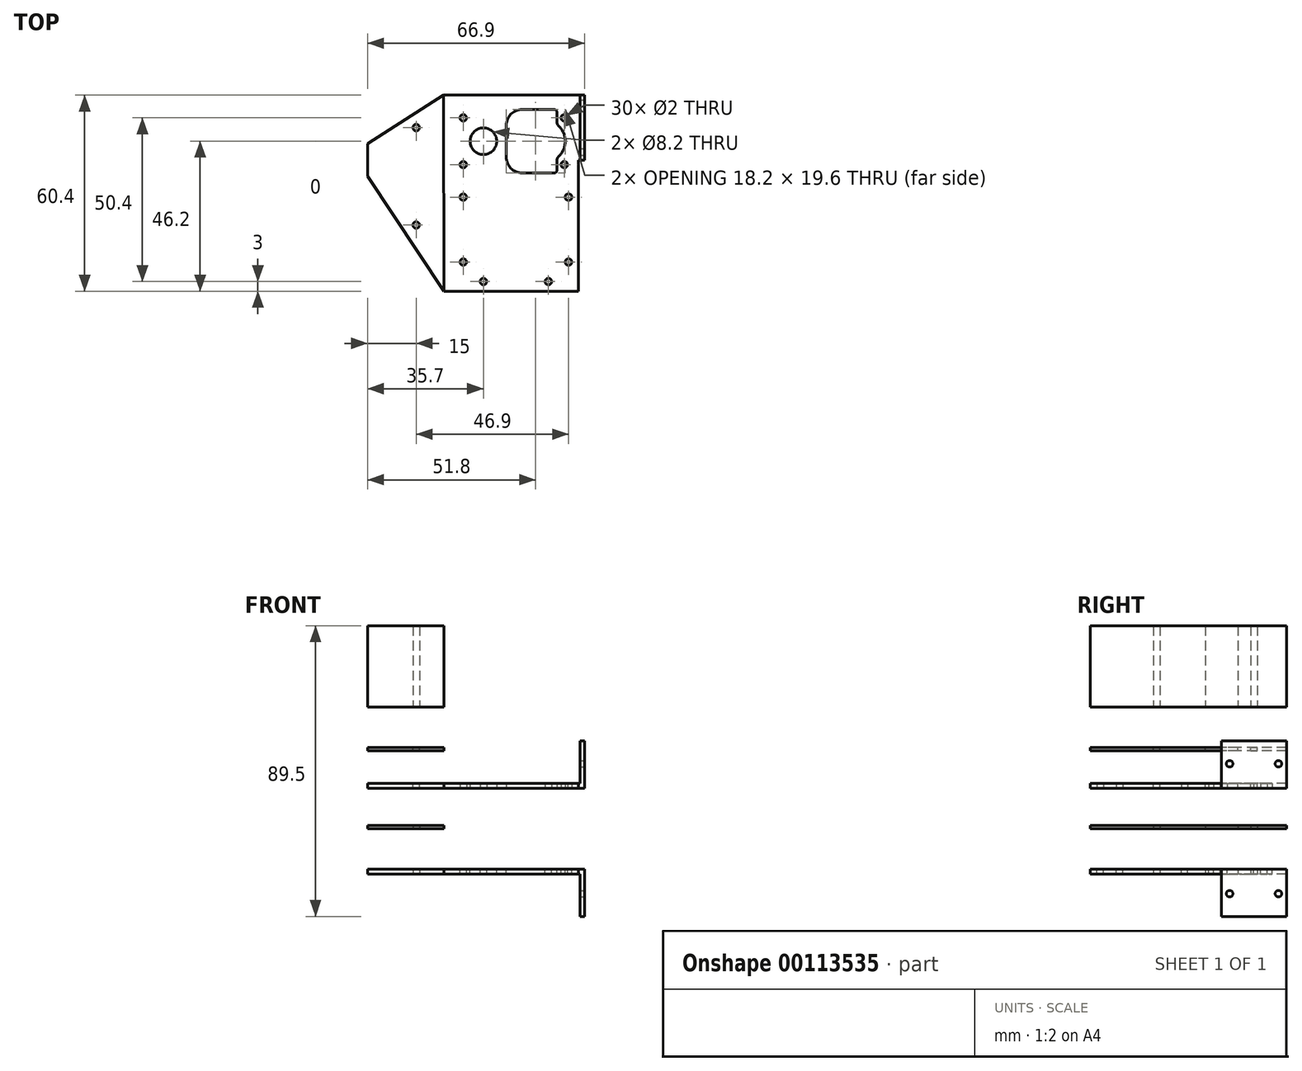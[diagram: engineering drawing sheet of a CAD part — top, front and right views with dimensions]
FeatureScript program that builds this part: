
annotation { "Feature Type Name" : "Feature", "Feature Type Description" : "" }
export const myFeature = defineFeature(function(context is Context, id is Id, definition is map)
    precondition{}
    {
        {
            var Q0;
            Q0=qCreatedBy(makeId("Top.planeOp"),FACE);
            var sketch = newSketch(context, id + "F0", { "sketchPlane" : qUnion([Q0])});
            skLineSegment(sketch, "E0.top", {"start": v(19.2, 14.2) * mm, "end": v(-19.2, 14.2) * mm});
            skLineSegment(sketch, "E0.left", {"start": v(19.2, -14.2) * mm, "end": v(19.2, 14.2) * mm});
            skLineSegment(sketch, "E0.right", {"start": v(-19.2, -14.2) * mm, "end": v(-19.2, 14.2) * mm});
            skPoint(sketch, "E0.middle", {"position": v(0, 0) * mm});
            skCircle(sketch, "E1", {"center": v(-10, 0) * mm, "radius": 4.1 * mm});
            skCircle(sketch, "E2", {"center": v(-16.2, 7.2) * mm, "radius": 1 * mm});
            skCircle(sketch, "E3", {"center": v(14.9, 7.2) * mm, "radius": 1 * mm});
            skLineSegment(sketch, "E4.bottom", {"start": v(2, 9.8) * mm, "end": v(11.7, 9.8) * mm});
            skLineSegment(sketch, "E4.top", {"start": v(2, -9.8) * mm, "end": v(11.7, -9.8) * mm});
            skLineSegment(sketch, "E4.left", {"start": v(-3, 4.8) * mm, "end": v(-3, -4.8) * mm});
            skLineSegment(sketch, "E4.right", {"start": v(12.7, 8.8) * mm, "end": v(12.7, 5.6) * mm});
            skPoint(sketch, "E4.middle", {"position": v(4.85, 0) * mm});
            skPoint(sketch, "E5.visualSharp", {"position": v(-3, 9.8) * mm});
            skArc(sketch, "E5.filletArc", {"start": v(2, 9.8) * mm, "mid": v(-1.54, 8.34) * mm, "end": v(-3, 4.8) * mm});
            skPoint(sketch, "E6.visualSharp", {"position": v(-3, -9.8) * mm});
            skArc(sketch, "E6.filletArc", {"start": v(-3, -4.8) * mm, "mid": v(-1.54, -8.34) * mm, "end": v(2, -9.8) * mm});
            skPoint(sketch, "E7.visualSharp", {"position": v(12.7, 9.8) * mm});
            skArc(sketch, "E7.filletArc", {"start": v(12.7, 8.8) * mm, "mid": v(12.4, 9.5) * mm, "end": v(11.7, 9.8) * mm});
            skPoint(sketch, "E8.visualSharp", {"position": v(12.7, -9.8) * mm});
            skArc(sketch, "E8.filletArc", {"start": v(11.7, -9.8) * mm, "mid": v(12.4, -9.5) * mm, "end": v(12.7, -8.8) * mm});
            skCircle(sketch, "E9.MirrorC", {"center": v(-16.2, -7.2) * mm, "radius": 1 * mm});
            skCircle(sketch, "E10.MirrorC", {"center": v(14.9, -7.2) * mm, "radius": 1 * mm});
            skArc(sketch, "E11", {"start": v(13.03, -4.84) * mm, "mid": v(15.2, 0) * mm, "end": v(13.03, 4.84) * mm});
            skLineSegment(sketch, "E12.trimOffspring", {"start": v(12.7, -5.6) * mm, "end": v(12.7, -8.8) * mm});
            skPoint(sketch, "E13.visualSharp", {"position": v(12.7, 5.12) * mm});
            skArc(sketch, "E13.filletArc", {"start": v(12.7, 5.6) * mm, "mid": v(12.79, 5.18) * mm, "end": v(13.03, 4.84) * mm});
            skPoint(sketch, "E14.visualSharp", {"position": v(12.7, -5.12) * mm});
            skArc(sketch, "E14.filletArc", {"start": v(13.03, -4.84) * mm, "mid": v(12.79, -5.18) * mm, "end": v(12.7, -5.6) * mm});
            skLineSegment(sketch, "E15.bottom", {"start": v(-19.2, -14.2) * mm, "end": v(19.2, -14.2) * mm, "construction": true});
            skLineSegment(sketch, "E15.top", {"start": v(-19.2, -46.2) * mm, "end": v(19.2, -46.2) * mm});
            skLineSegment(sketch, "E15.left", {"start": v(-19.2, -14.2) * mm, "end": v(-19.2, -46.2) * mm});
            skLineSegment(sketch, "E15.right", {"start": v(19.2, -14.2) * mm, "end": v(19.2, -46.2) * mm});
            skCircle(sketch, "E16", {"center": v(-10, -43.2) * mm, "radius": 1 * mm});
            skCircle(sketch, "E17.MirrorC", {"center": v(10, -43.2) * mm, "radius": 1 * mm});
            skCircle(sketch, "E18", {"center": v(16.2, -37.2) * mm, "radius": 1 * mm});
            skCircle(sketch, "E19", {"center": v(16.2, -17.2) * mm, "radius": 1 * mm});
            skCircle(sketch, "E20.MirrorC", {"center": v(-16.2, -17.2) * mm, "radius": 1 * mm});
            skCircle(sketch, "E21.MirrorC", {"center": v(-16.2, -37.2) * mm, "radius": 1 * mm});
            skCircle(sketch, "E22", {"center": v(0, -30.2) * mm, "radius": 12.5 * mm, "construction": true});
            skSolve(sketch);
        }
        {
            var Q0;
            Q0=qSketchRegion(id+"F0",true);
            extrude(context, id + "F1", {"entities" : qUnion([Q0]), "depth" : 1.5 * mm});
        }
        {
            var Q0;
            Q0=makeQuery(id+"F1.opExtrude","SWEPT_FACE",FACE,{"disambiguationData":[OSD([sQuery(id+"F0.wireOp",EDGE,"E0.left"),sQuery(id+"F0.wireOp",EDGE,"E15.right")])]});
            var sketch = newSketch(context, id + "F2", { "sketchPlane" : qUnion([Q0])});
            skLineSegment(sketch, "E23.bottom", {"start": v(14.2, 0) * mm, "end": v(-5.8, 0) * mm});
            skLineSegment(sketch, "E23.top", {"start": v(14.2, 1.5) * mm, "end": v(-5.8, 1.5) * mm});
            skLineSegment(sketch, "E23.left", {"start": v(14.2, 0) * mm, "end": v(14.2, 1.5) * mm});
            skLineSegment(sketch, "E23.right", {"start": v(-5.8, 0) * mm, "end": v(-5.8, 1.5) * mm});
            skSolve(sketch);
        }
        {
            var Q0;
            Q0=qSketchRegion(id+"F2",true);
            extrude(context, id + "F3", {"entities" : qUnion([Q0]), "operationType" : NewBodyOperationType.ADD, "depth" : 2 * mm});
        }
        {
            var Q0;
            Q0=makeQuery(id+"F3.boolean.opBoolean","MERGE",FACE,{"derivedFrom":[makeQuery(id+"F1.opExtrude","CAP_FACE",FACE,{"disambiguationData":[OSD([sQuery(id+"F0.wireOp",EDGE,"E0.top"),sQuery(id+"F0.wireOp",EDGE,"E0.left"),sQuery(id+"F0.wireOp",EDGE,"E0.right"),sQuery(id+"F0.wireOp",EDGE,"E1"),sQuery(id+"F0.wireOp",EDGE,"E2"),sQuery(id+"F0.wireOp",EDGE,"E3"),sQuery(id+"F0.wireOp",EDGE,"E4.bottom"),sQuery(id+"F0.wireOp",EDGE,"E4.top"),sQuery(id+"F0.wireOp",EDGE,"E4.left"),sQuery(id+"F0.wireOp",EDGE,"E4.right"),sQuery(id+"F0.wireOp",EDGE,"E5.filletArc"),sQuery(id+"F0.wireOp",EDGE,"E6.filletArc"),sQuery(id+"F0.wireOp",EDGE,"E7.filletArc"),sQuery(id+"F0.wireOp",EDGE,"E8.filletArc"),sQuery(id+"F0.wireOp",EDGE,"E9.MirrorC"),sQuery(id+"F0.wireOp",EDGE,"E10.MirrorC"),sQuery(id+"F0.wireOp",EDGE,"E11"),sQuery(id+"F0.wireOp",EDGE,"E12.trimOffspring"),sQuery(id+"F0.wireOp",EDGE,"E13.filletArc"),sQuery(id+"F0.wireOp",EDGE,"E14.filletArc"),sQuery(id+"F0.wireOp",EDGE,"E15.top"),sQuery(id+"F0.wireOp",EDGE,"E15.left"),sQuery(id+"F0.wireOp",EDGE,"E15.right"),sQuery(id+"F0.wireOp",EDGE,"E16"),sQuery(id+"F0.wireOp",EDGE,"E17.MirrorC"),sQuery(id+"F0.wireOp",EDGE,"E18"),sQuery(id+"F0.wireOp",EDGE,"E19"),sQuery(id+"F0.wireOp",EDGE,"E20.MirrorC"),sQuery(id+"F0.wireOp",EDGE,"E21.MirrorC")])],"isStart":false}),makeQuery(id+"F3.opExtrude","SWEPT_FACE",FACE,{"disambiguationData":[OSD([sQuery(id+"F2.wireOp",EDGE,"E23.top")])]})]});
            var sketch = newSketch(context, id + "F4", { "sketchPlane" : qUnion([Q0])});
            skLineSegment(sketch, "E24.bottom", {"start": v(19.7, 14.2) * mm, "end": v(21.2, 14.2) * mm});
            skLineSegment(sketch, "E24.top", {"start": v(19.7, -5.8) * mm, "end": v(21.2, -5.8) * mm});
            skLineSegment(sketch, "E24.left", {"start": v(19.7, 14.2) * mm, "end": v(19.7, -5.8) * mm});
            skLineSegment(sketch, "E24.right", {"start": v(21.2, 14.2) * mm, "end": v(21.2, -5.8) * mm});
            skSolve(sketch);
        }
        {
            var Q0;
            Q0=qSketchRegion(id+"F4",true);
            extrude(context, id + "F5", {"entities" : qUnion([Q0]), "operationType" : NewBodyOperationType.ADD, "depth" : 13 * mm});
        }
        {
            var Q0;
            Q0=qCreatedBy(makeId("Top.planeOp"),FACE);
            cPlane(context, id + "F6", {"entities" : qUnion([Q0]), "cplaneType" : CPlaneType.OFFSET, "offset" : (25 / 2) * mm, "oppositeDirection" : true, "width" : 150 * mm, "height" : 150 * mm});
        }
        {
            var Q0;
            Q0=makeQuery(id+"F1.opExtrude","SWEPT_BODY",BODY,{"disambiguationData":[OSD([sQuery(id+"F0.wireOp",EDGE,"E0.top"),sQuery(id+"F0.wireOp",EDGE,"E0.left"),sQuery(id+"F0.wireOp",EDGE,"E0.right"),sQuery(id+"F0.wireOp",EDGE,"E1"),sQuery(id+"F0.wireOp",EDGE,"E2"),sQuery(id+"F0.wireOp",EDGE,"E3"),sQuery(id+"F0.wireOp",EDGE,"E4.bottom"),sQuery(id+"F0.wireOp",EDGE,"E4.top"),sQuery(id+"F0.wireOp",EDGE,"E4.left"),sQuery(id+"F0.wireOp",EDGE,"E4.right"),sQuery(id+"F0.wireOp",EDGE,"E5.filletArc"),sQuery(id+"F0.wireOp",EDGE,"E6.filletArc"),sQuery(id+"F0.wireOp",EDGE,"E7.filletArc"),sQuery(id+"F0.wireOp",EDGE,"E8.filletArc"),sQuery(id+"F0.wireOp",EDGE,"E9.MirrorC"),sQuery(id+"F0.wireOp",EDGE,"E10.MirrorC"),sQuery(id+"F0.wireOp",EDGE,"E11"),sQuery(id+"F0.wireOp",EDGE,"E12.trimOffspring"),sQuery(id+"F0.wireOp",EDGE,"E13.filletArc"),sQuery(id+"F0.wireOp",EDGE,"E14.filletArc"),sQuery(id+"F0.wireOp",EDGE,"E15.top"),sQuery(id+"F0.wireOp",EDGE,"E15.left"),sQuery(id+"F0.wireOp",EDGE,"E15.right"),sQuery(id+"F0.wireOp",EDGE,"E16"),sQuery(id+"F0.wireOp",EDGE,"E17.MirrorC"),sQuery(id+"F0.wireOp",EDGE,"E18"),sQuery(id+"F0.wireOp",EDGE,"E19"),sQuery(id+"F0.wireOp",EDGE,"E20.MirrorC"),sQuery(id+"F0.wireOp",EDGE,"E21.MirrorC")])]});
            var Q1;
            Q1=qCreatedBy(id+"F6.planeOp",FACE);
            mirror(context, id + "F7", {"entities" : qUnion([Q0]), "mirrorPlane" : qUnion([Q1])});
        }
        {
            var Q0;
            Q0=makeQuery(id+"F7.opPattern","COPY",FACE,{"derivedFrom":makeQuery(id+"F5.boolean.opBoolean","MERGE",FACE,{"derivedFrom":[makeQuery(id+"F3.opExtrude","CAP_FACE",FACE,{"disambiguationData":[OSD([sQuery(id+"F2.wireOp",EDGE,"E23.bottom"),sQuery(id+"F2.wireOp",EDGE,"E23.top"),sQuery(id+"F2.wireOp",EDGE,"E23.left"),sQuery(id+"F2.wireOp",EDGE,"E23.right")])],"isStart":false}),makeQuery(id+"F5.opExtrude","SWEPT_FACE",FACE,{"disambiguationData":[OSD([sQuery(id+"F4.wireOp",EDGE,"E24.right")])]})]}),"instanceName":"1"});
            var sketch = newSketch(context, id + "F8", { "sketchPlane" : qUnion([Q0])});
            skCircle(sketch, "E25", {"center": v(11.7, 7.5) * mm, "radius": 1 * mm});
            skCircle(sketch, "E26", {"center": v(-3.3, 7.5) * mm, "radius": 1 * mm});
            skCircle(sketch, "E27.MirrorC", {"center": v(11.7, -32.5) * mm, "radius": 1 * mm});
            skCircle(sketch, "E28.MirrorC", {"center": v(-3.3, -32.5) * mm, "radius": 1 * mm});
            skSolve(sketch);
        }
        {
            var Q0;
            Q0=qSketchRegion(id+"F8",true);
            extrude(context, id + "F9", {"entities" : qUnion([Q0]), "operationType" : NewBodyOperationType.REMOVE, "endBound" : BoundingType.UP_TO_NEXT, "oppositeDirection" : true, "depth" : 25 * mm});
        }
        {
            var Q0;
            Q0=makeQuery(id+"F1.opExtrude","SWEPT_FACE",FACE,{"disambiguationData":[OSD([sQuery(id+"F0.wireOp",EDGE,"E0.right"),sQuery(id+"F0.wireOp",EDGE,"E15.left")])]});
            var sketch = newSketch(context, id + "F10", { "sketchPlane" : qUnion([Q0])});
            skLineSegment(sketch, "E29.bottom", {"start": v(-14.2, 0) * mm, "end": v(46.2, 0) * mm});
            skLineSegment(sketch, "E29.top", {"start": v(-14.2, 1.5) * mm, "end": v(46.2, 1.5) * mm});
            skLineSegment(sketch, "E29.left", {"start": v(-14.2, 0) * mm, "end": v(-14.2, 1.5) * mm});
            skLineSegment(sketch, "E29.right", {"start": v(46.2, 0) * mm, "end": v(46.2, 1.5) * mm});
            skSolve(sketch);
        }
        {
            var Q0;
            Q0=qSketchRegion(id+"F10",true);
            extrude(context, id + "F11", {"entities" : qUnion([Q0]), "operationType" : NewBodyOperationType.ADD, "depth" : (25 + 1.5) * mm});
        }
        {
            var Q0;
            Q0=makeQuery(id+"F11.boolean.opBoolean","MERGE",FACE,{"derivedFrom":[makeQuery(id+"F3.boolean.opBoolean","MERGE",FACE,{"derivedFrom":[makeQuery(id+"F1.opExtrude","CAP_FACE",FACE,{"disambiguationData":[OSD([sQuery(id+"F0.wireOp",EDGE,"E0.top"),sQuery(id+"F0.wireOp",EDGE,"E0.left"),sQuery(id+"F0.wireOp",EDGE,"E0.right"),sQuery(id+"F0.wireOp",EDGE,"E1"),sQuery(id+"F0.wireOp",EDGE,"E2"),sQuery(id+"F0.wireOp",EDGE,"E3"),sQuery(id+"F0.wireOp",EDGE,"E4.bottom"),sQuery(id+"F0.wireOp",EDGE,"E4.top"),sQuery(id+"F0.wireOp",EDGE,"E4.left"),sQuery(id+"F0.wireOp",EDGE,"E4.right"),sQuery(id+"F0.wireOp",EDGE,"E5.filletArc"),sQuery(id+"F0.wireOp",EDGE,"E6.filletArc"),sQuery(id+"F0.wireOp",EDGE,"E7.filletArc"),sQuery(id+"F0.wireOp",EDGE,"E8.filletArc"),sQuery(id+"F0.wireOp",EDGE,"E9.MirrorC"),sQuery(id+"F0.wireOp",EDGE,"E10.MirrorC"),sQuery(id+"F0.wireOp",EDGE,"E11"),sQuery(id+"F0.wireOp",EDGE,"E12.trimOffspring"),sQuery(id+"F0.wireOp",EDGE,"E13.filletArc"),sQuery(id+"F0.wireOp",EDGE,"E14.filletArc"),sQuery(id+"F0.wireOp",EDGE,"E15.top"),sQuery(id+"F0.wireOp",EDGE,"E15.left"),sQuery(id+"F0.wireOp",EDGE,"E15.right"),sQuery(id+"F0.wireOp",EDGE,"E16"),sQuery(id+"F0.wireOp",EDGE,"E17.MirrorC"),sQuery(id+"F0.wireOp",EDGE,"E18"),sQuery(id+"F0.wireOp",EDGE,"E19"),sQuery(id+"F0.wireOp",EDGE,"E20.MirrorC"),sQuery(id+"F0.wireOp",EDGE,"E21.MirrorC")])],"isStart":false}),makeQuery(id+"F3.opExtrude","SWEPT_FACE",FACE,{"disambiguationData":[OSD([sQuery(id+"F2.wireOp",EDGE,"E23.top")])]})]}),makeQuery(id+"F11.opExtrude","SWEPT_FACE",FACE,{"disambiguationData":[OSD([sQuery(id+"F10.wireOp",EDGE,"E29.top")])]})]});
            var sketch = newSketch(context, id + "F12", { "sketchPlane" : qUnion([Q0])});
            skLineSegment(sketch, "E30", {"start": v(-20.7, 14.2) * mm, "end": v(-20.7, -46.2) * mm, "construction": true});
            skLineSegment(sketch, "E31", {"start": v(-22.25, 14.2) * mm, "end": v(-45.7, -0.8) * mm});
            skLineSegment(sketch, "E32", {"start": v(-45.7, -0.8) * mm, "end": v(-45.7, -10.8) * mm});
            skLineSegment(sketch, "E33", {"start": v(-45.7, -10.8) * mm, "end": v(-22.2, -46.2) * mm});
            skLineSegment(sketch, "E34", {"start": v(-22.2, -46.2) * mm, "end": v(-45.7, -46.2) * mm});
            skLineSegment(sketch, "E35", {"start": v(-45.7, -46.2) * mm, "end": v(-45.7, -10.8) * mm});
            skLineSegment(sketch, "E36", {"start": v(-22.25, 14.2) * mm, "end": v(-45.7, 14.2) * mm});
            skLineSegment(sketch, "E37", {"start": v(-45.7, 14.2) * mm, "end": v(-45.7, -0.8) * mm});
            skCircle(sketch, "E38", {"center": v(-30.7, 4.2) * mm, "radius": 1 * mm});
            skCircle(sketch, "E39", {"center": v(-30.7, -25.8) * mm, "radius": 1 * mm});
            skLineSegment(sketch, "E40", {"start": v(-30.7, 4.2) * mm, "end": v(-30.7, -25.8) * mm, "construction": true});
            skSolve(sketch);
        }
        {
            var Q0;
            Q0=qSketchRegion(id+"F12",true);
            extrude(context, id + "F13", {"entities" : qUnion([Q0]), "operationType" : NewBodyOperationType.REMOVE, "endBound" : BoundingType.UP_TO_NEXT, "oppositeDirection" : true, "depth" : 25 * mm});
        }
        {
            var Q0;
            Q0=makeQuery(id+"F1.opExtrude","SWEPT_BODY",BODY,{"disambiguationData":[OSD([sQuery(id+"F0.wireOp",EDGE,"E0.top"),sQuery(id+"F0.wireOp",EDGE,"E0.left"),sQuery(id+"F0.wireOp",EDGE,"E0.right"),sQuery(id+"F0.wireOp",EDGE,"E1"),sQuery(id+"F0.wireOp",EDGE,"E2"),sQuery(id+"F0.wireOp",EDGE,"E3"),sQuery(id+"F0.wireOp",EDGE,"E4.bottom"),sQuery(id+"F0.wireOp",EDGE,"E4.top"),sQuery(id+"F0.wireOp",EDGE,"E4.left"),sQuery(id+"F0.wireOp",EDGE,"E4.right"),sQuery(id+"F0.wireOp",EDGE,"E5.filletArc"),sQuery(id+"F0.wireOp",EDGE,"E6.filletArc"),sQuery(id+"F0.wireOp",EDGE,"E7.filletArc"),sQuery(id+"F0.wireOp",EDGE,"E8.filletArc"),sQuery(id+"F0.wireOp",EDGE,"E9.MirrorC"),sQuery(id+"F0.wireOp",EDGE,"E10.MirrorC"),sQuery(id+"F0.wireOp",EDGE,"E11"),sQuery(id+"F0.wireOp",EDGE,"E12.trimOffspring"),sQuery(id+"F0.wireOp",EDGE,"E13.filletArc"),sQuery(id+"F0.wireOp",EDGE,"E14.filletArc"),sQuery(id+"F0.wireOp",EDGE,"E15.top"),sQuery(id+"F0.wireOp",EDGE,"E15.left"),sQuery(id+"F0.wireOp",EDGE,"E15.right"),sQuery(id+"F0.wireOp",EDGE,"E16"),sQuery(id+"F0.wireOp",EDGE,"E17.MirrorC"),sQuery(id+"F0.wireOp",EDGE,"E18"),sQuery(id+"F0.wireOp",EDGE,"E19"),sQuery(id+"F0.wireOp",EDGE,"E20.MirrorC"),sQuery(id+"F0.wireOp",EDGE,"E21.MirrorC")])]});
            var Q1;
            Q1=qCreatedBy(id+"F6.planeOp",FACE);
            mirror(context, id + "F14", {"operationType" : NewBodyOperationType.ADD, "entities" : qUnion([Q0]), "mirrorPlane" : qUnion([Q1])});
        }
        {
            var Q0;
            Q0=qCreatedBy(makeId("Top.planeOp"),FACE);
            cPlane(context, id + "F15", {"entities" : qUnion([Q0]), "cplaneType" : CPlaneType.OFFSET, "offset" : 25 * mm, "width" : 150 * mm, "height" : 150 * mm});
        }
        {
            var Q0;
            Q0=qCreatedBy(id+"F15.planeOp",FACE);
            var sketch = newSketch(context, id + "F16", { "sketchPlane" : qUnion([Q0])});
            skLineSegment(sketch, "E41.0.0", {"start": v(19.7, 14.2) * mm, "end": v(-22.25, 14.2) * mm, "construction": true});
            skLineSegment(sketch, "E41.0.1", {"start": v(-22.25, 14.2) * mm, "end": v(-45.7, -0.8) * mm});
            skLineSegment(sketch, "E41.0.2", {"start": v(-45.7, -0.8) * mm, "end": v(-45.7, -10.8) * mm});
            skLineSegment(sketch, "E41.0.3", {"start": v(-45.7, -10.8) * mm, "end": v(-22.2, -46.2) * mm});
            skLineSegment(sketch, "E41.0.4", {"start": v(-22.2, -46.2) * mm, "end": v(19.2, -46.2) * mm, "construction": true});
            skLineSegment(sketch, "E41.0.5", {"start": v(19.2, -46.2) * mm, "end": v(19.2, -5.8) * mm, "construction": true});
            skLineSegment(sketch, "E41.0.6", {"start": v(19.2, -5.8) * mm, "end": v(19.7, -5.8) * mm, "construction": true});
            skLineSegment(sketch, "E41.0.7", {"start": v(19.7, -5.8) * mm, "end": v(19.7, 14.2) * mm, "construction": true});
            skLineSegment(sketch, "E42", {"start": v(-22.25, 14.2) * mm, "end": v(-22.2, -46.2) * mm});
            skCircle(sketch, "E43.0", {"center": v(-30.7, 4.2) * mm, "radius": 1 * mm});
            skCircle(sketch, "E43.1", {"center": v(-30.7, -25.8) * mm, "radius": 1 * mm});
            skCircle(sketch, "E43.2", {"center": v(-30.7, 4.2) * mm, "radius": 1 * mm});
            skCircle(sketch, "E43.3", {"center": v(-30.7, -25.8) * mm, "radius": 1 * mm});
            skCircle(sketch, "E43.4", {"center": v(-30.7, 4.2) * mm, "radius": 1 * mm});
            skCircle(sketch, "E43.5", {"center": v(-30.7, -25.8) * mm, "radius": 1 * mm});
            skCircle(sketch, "E43.6", {"center": v(-30.7, -25.8) * mm, "radius": 1 * mm});
            skCircle(sketch, "E43.7", {"center": v(-30.7, 4.2) * mm, "radius": 1 * mm});
            skSolve(sketch);
        }
        {
            var Q0;
            Q0=qSketchRegion(id+"F16",true);
            extrude(context, id + "F17", {"entities" : qUnion([Q0]), "depth" : 25 * mm});
        }
        {
            var Q0;
            Q0=qCreatedBy(id+"F6.planeOp",FACE);
            var sketch = newSketch(context, id + "F18", { "sketchPlane" : qUnion([Q0])});
            skLineSegment(sketch, "E44.0", {"start": v(-22.25, 14.2) * mm, "end": v(-45.7, -0.8) * mm});
            skLineSegment(sketch, "E45.0", {"start": v(-45.7, -0.8) * mm, "end": v(-45.7, -10.8) * mm});
            skLineSegment(sketch, "E46.0", {"start": v(-45.7, -10.8) * mm, "end": v(-22.2, -46.2) * mm});
            skLineSegment(sketch, "E47.0", {"start": v(-22.25, 14.2) * mm, "end": v(-22.2, -46.2) * mm});
            skLineSegment(sketch, "E48", {"start": v(-45.7, -5.8) * mm, "end": v(-22.23, -5.8) * mm, "construction": true});
            skCircle(sketch, "E49", {"center": v(-25.24, 4.2) * mm, "radius": 1.1 * mm, "construction": true});
            skCircle(sketch, "E50.MirrorC", {"center": v(-25.24, -15.8) * mm, "radius": 1.1 * mm, "construction": true});
            skCircle(sketch, "E51.0", {"center": v(-30.7, 4.2) * mm, "radius": 1 * mm});
            skCircle(sketch, "E52.0", {"center": v(-30.7, -25.8) * mm, "radius": 1 * mm});
            skSolve(sketch);
        }
        {
            var Q0;
            Q0 = qSketchRegion(id + "F18", true);
            extrude(context, id + "F19", {"entities" : qUnion([Q0]), "depth" : 1 * mm});
        }
        {
            var Q0;
            Q0=makeQuery(id+"F19.opExtrude","SWEPT_BODY",BODY,{"disambiguationData":[OSD([sQuery(id+"F18.wireOp",EDGE,"E44.0"),sQuery(id+"F18.wireOp",EDGE,"E45.0"),sQuery(id+"F18.wireOp",EDGE,"E46.0"),sQuery(id+"F18.wireOp",EDGE,"E47.0"),sQuery(id+"F18.wireOp",EDGE,"E49"),sQuery(id+"F18.wireOp",EDGE,"E50.MirrorC"),sQuery(id+"F18.wireOp",EDGE,"E51.0"),sQuery(id+"F18.wireOp",EDGE,"E52.0")])]});
            var Q1;
            Q1=qCreatedBy(makeId("Top.planeOp"),FACE);
            mirror(context, id + "F20", {"entities" : qUnion([Q0]), "mirrorPlane" : qUnion([Q1])});
        }
    });
